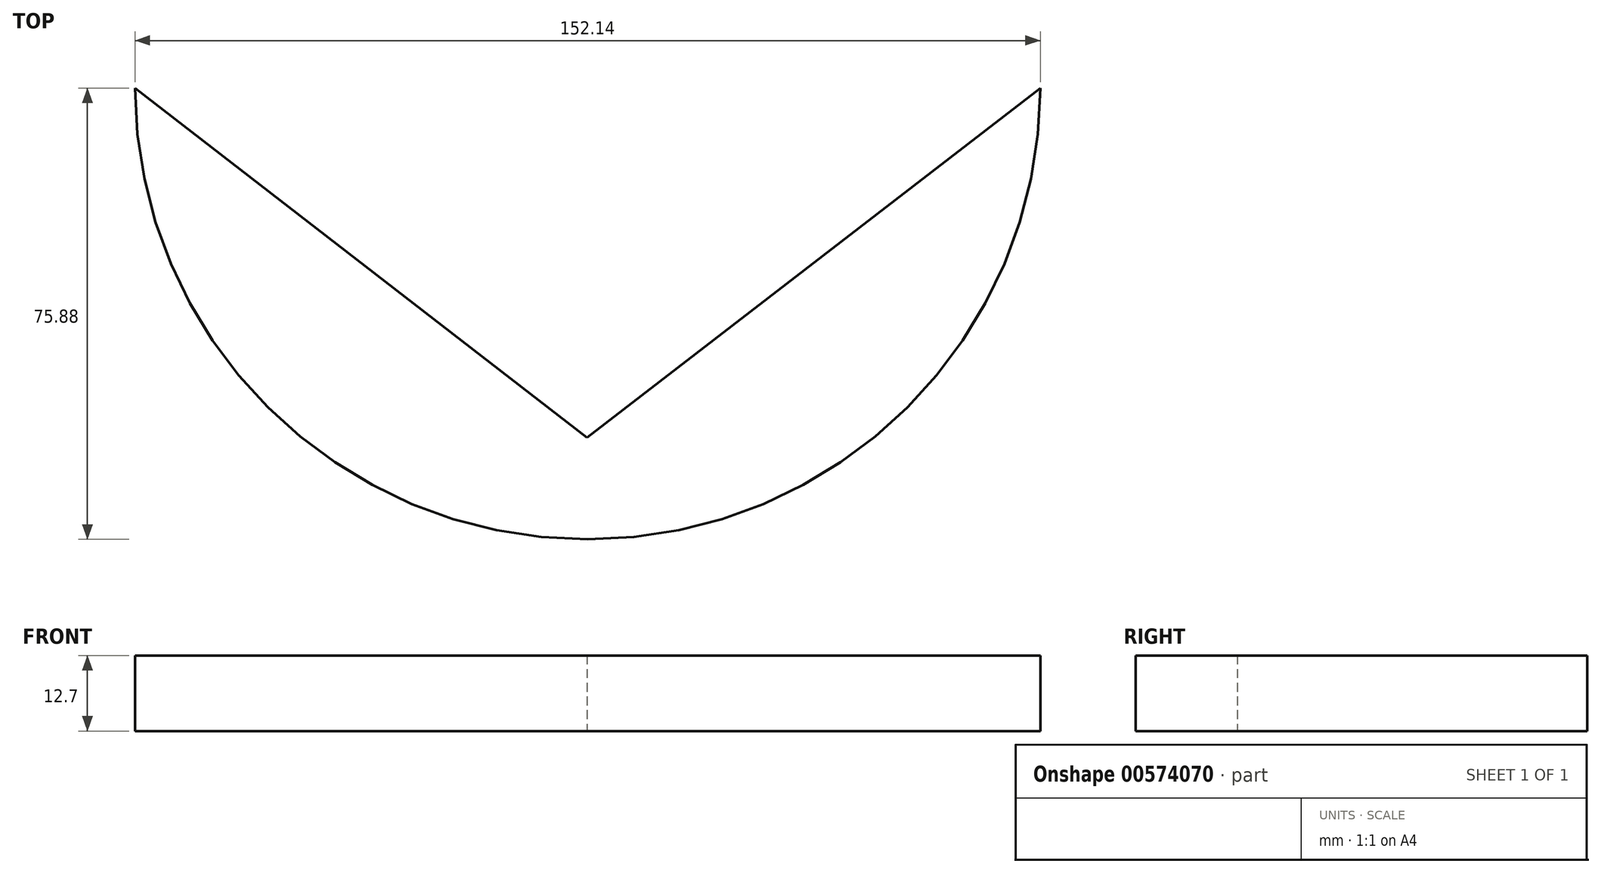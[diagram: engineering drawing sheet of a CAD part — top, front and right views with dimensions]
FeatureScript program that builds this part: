
annotation { "Feature Type Name" : "Feature", "Feature Type Description" : "" }
export const myFeature = defineFeature(function(context is Context, id is Id, definition is map)
    precondition{}
    {
        {
            var Q0;
            Q0=qCreatedBy(makeId("Top.planeOp"),FACE);
            var sketch = newSketch(context, id + "F0", { "sketchPlane" : qUnion([Q0])});
            skArc(sketch, "E0", {"start": v(-75.95, 0) * mm, "mid": v(0.12, -75.88) * mm, "end": v(76.19, 0) * mm});
            skLineSegment(sketch, "E1", {"start": v(-75.95, 0) * mm, "end": v(0, -58.75) * mm});
            skLineSegment(sketch, "E2", {"start": v(76.19, 0) * mm, "end": v(0, -58.75) * mm});
            skSolve(sketch);
        }
        {
            var Q0;
            Q0 = qSketchRegion(id + "F0", true);
            extrude(context, id + "F1", {"entities" : qUnion([Q0]), "depth" : 12.7 * mm, "offsetDistance" : 25.4 * mm});
        }
    });
